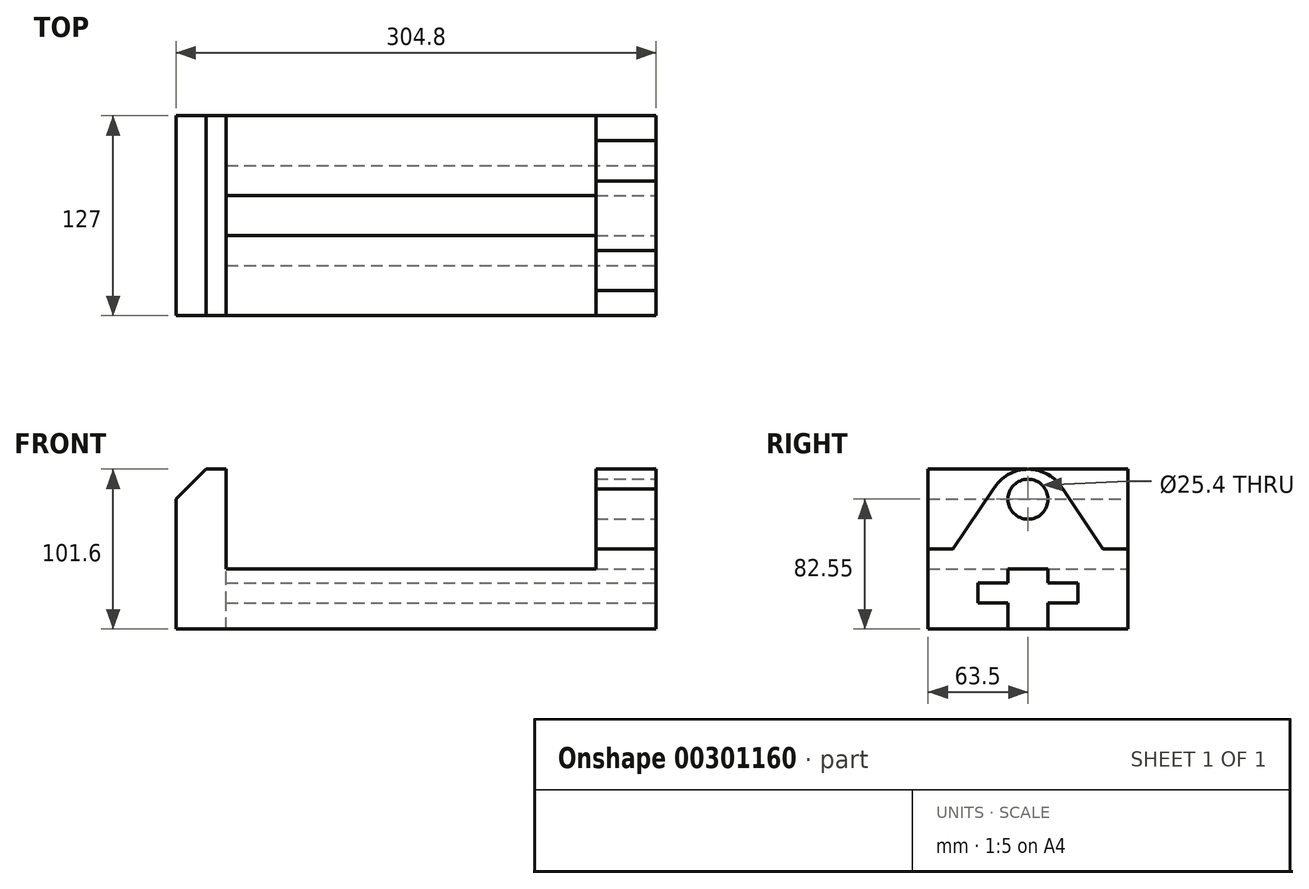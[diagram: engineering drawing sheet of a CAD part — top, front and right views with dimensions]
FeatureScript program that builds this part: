
annotation { "Feature Type Name" : "Feature", "Feature Type Description" : "" }
export const myFeature = defineFeature(function(context is Context, id is Id, definition is map)
    precondition{}
    {
        {
            var Q0;
            Q0=qCreatedBy(makeId("Front.planeOp"),FACE);
            var sketch = newSketch(context, id + "F0", { "sketchPlane" : qUnion([Q0])});
            skLineSegment(sketch, "E0", {"start": v(0, 0) * mm, "end": v(304.8, 0) * mm});
            skLineSegment(sketch, "E1", {"start": v(304.8, 0) * mm, "end": v(304.8, 101.6) * mm});
            skLineSegment(sketch, "E2", {"start": v(304.8, 101.6) * mm, "end": v(266.7, 101.6) * mm});
            skLineSegment(sketch, "E3", {"start": v(266.7, 101.6) * mm, "end": v(266.7, 38.1) * mm});
            skLineSegment(sketch, "E4", {"start": v(266.7, 38.1) * mm, "end": v(31.75, 38.1) * mm});
            skLineSegment(sketch, "E5", {"start": v(31.75, 38.1) * mm, "end": v(31.75, 101.6) * mm});
            skLineSegment(sketch, "E6", {"start": v(31.75, 101.6) * mm, "end": v(0, 101.6) * mm});
            skLineSegment(sketch, "E7", {"start": v(0, 101.6) * mm, "end": v(0, 0) * mm});
            skLineSegment(sketch, "E8", {"start": v(0, 101.6) * mm, "end": v(19.05, 101.6) * mm});
            skLineSegment(sketch, "E9", {"start": v(19.05, 101.6) * mm, "end": v(0, 82.55) * mm});
            skLineSegment(sketch, "E10", {"start": v(0, 82.55) * mm, "end": v(0, 101.6) * mm});
            skSolve(sketch);
        }
        {
            var Q0;
            Q0=makeQuery(id+"F0.imprint","IMPRINT",FACE,{"disambiguationData":[TD([[makeQuery(id+"F0.imprint","IMPRINT",EDGE,{"derivedFrom":sQuery(id+"F0.wireOp",EDGE,"E0")}),1.0]])]});
            extrude(context, id + "F1", {"entities" : qUnion([Q0]), "depth" : 127 * mm});
        }
        {
            var Q0;
            Q0=makeQuery(id+"F1.opExtrude","SWEPT_FACE",FACE,{"disambiguationData":[OSD([sQuery(id+"F0.wireOp",EDGE,"E1")])]});
            var sketch = newSketch(context, id + "F2", { "sketchPlane" : qUnion([Q0])});
            skLineSegment(sketch, "E11", {"start": v(-127, 50.8) * mm, "end": v(-111.12, 50.8) * mm});
            skLineSegment(sketch, "E12", {"start": v(0, 50.8) * mm, "end": v(-15.88, 50.8) * mm});
            skLineSegment(sketch, "E13", {"start": v(-111.12, 50.8) * mm, "end": v(-85.5, 88.9) * mm});
            skLineSegment(sketch, "E14", {"start": v(-15.87, 50.8) * mm, "end": v(-41.5, 88.9) * mm});
            skArc(sketch, "E15", {"start": v(-41.5, 88.9) * mm, "mid": v(-63.5, 101.6) * mm, "end": v(-85.5, 88.9) * mm});
            skSolve(sketch);
        }
        {
            var Q0;
            Q0 = qSketchRegion(id + "F2", true);
            var Q1;
            {var subQ7=sQuery(id+"F2.wireOp",EDGE,"E11");Q1=makeQuery(id+"F2.imprint","IMPRINT",FACE,{"disambiguationData":[TD([[makeQuery(id+"F2.imprint","IMPRINT",EDGE,{"derivedFrom":subQ7}),1.0]])]});}
            var Q2;
            {var subQ7=sQuery(id+"F2.wireOp",EDGE,"E12");Q2=makeQuery(id+"F2.imprint","IMPRINT",FACE,{"disambiguationData":[TD([[makeQuery(id+"F2.imprint","IMPRINT",EDGE,{"derivedFrom":subQ7}),-1.0]])]});}
            extrude(context, id + "F3", {"entities" : qUnion([Q0, Q1, Q2]), "operationType" : NewBodyOperationType.REMOVE, "oppositeDirection" : true, "depth" : 38.1 * mm});
        }
        {
            var Q0;
            Q0=makeQuery(id+"F1.opExtrude","SWEPT_FACE",FACE,{"disambiguationData":[OSD([sQuery(id+"F0.wireOp",EDGE,"E1")])]});
            var sketch = newSketch(context, id + "F4", { "sketchPlane" : qUnion([Q0])});
            skLineSegment(sketch, "E16", {"start": v(-76.2, 0) * mm, "end": v(-76.2, 16.5) * mm});
            skLineSegment(sketch, "E17", {"start": v(-76.2, 16.5) * mm, "end": v(-95.25, 16.5) * mm});
            skLineSegment(sketch, "E18", {"start": v(-95.25, 16.5) * mm, "end": v(-95.25, 29.21) * mm});
            skLineSegment(sketch, "E19", {"start": v(-95.25, 29.21) * mm, "end": v(-76.2, 29.21) * mm});
            skLineSegment(sketch, "E20", {"start": v(-76.2, 29.21) * mm, "end": v(-76.2, 38.1) * mm});
            skLineSegment(sketch, "E21", {"start": v(-76.2, 38.1) * mm, "end": v(-50.8, 38.1) * mm});
            skLineSegment(sketch, "E22", {"start": v(-50.8, 38.1) * mm, "end": v(-50.8, 29.21) * mm});
            skLineSegment(sketch, "E23", {"start": v(-50.8, 29.21) * mm, "end": v(-31.75, 29.21) * mm});
            skLineSegment(sketch, "E24", {"start": v(-31.75, 29.21) * mm, "end": v(-31.75, 16.5) * mm});
            skLineSegment(sketch, "E25", {"start": v(-31.75, 16.5) * mm, "end": v(-50.8, 16.5) * mm});
            skLineSegment(sketch, "E26", {"start": v(-50.8, 16.5) * mm, "end": v(-50.8, 0) * mm});
            skSolve(sketch);
        }
        {
            var Q0;
            Q0 = qSketchRegion(id + "F4", true);
            var Q1;
            {var subQ0=sQuery(id+"F4.wireOp",EDGE,"E16");Q1=makeQuery(id+"F4.imprint","IMPRINT",FACE,{"disambiguationData":[TD([[makeQuery(id+"F4.imprint","IMPRINT",EDGE,{"derivedFrom":subQ0}),-1.0]])]});}
            extrude(context, id + "F5", {"entities" : qUnion([Q0, Q1]), "operationType" : NewBodyOperationType.REMOVE, "oppositeDirection" : true, "depth" : 273.05 * mm});
        }
        {
            var Q0;
            Q0=makeQuery(id+"F1.opExtrude","SWEPT_FACE",FACE,{"disambiguationData":[OSD([sQuery(id+"F0.wireOp",EDGE,"E1")])]});
            var sketch = newSketch(context, id + "F6", { "sketchPlane" : qUnion([Q0])});
            skCircle(sketch, "E27", {"center": v(-63.5, 82.55) * mm, "radius": 12.7 * mm});
            skSolve(sketch);
        }
        {
            var Q0;
            Q0 = qSketchRegion(id + "F6", true);
            extrude(context, id + "F7", {"entities" : qUnion([Q0]), "operationType" : NewBodyOperationType.REMOVE, "oppositeDirection" : true, "depth" : 38.1 * mm});
        }
    });
